# Revit family: Sink-Undermount-KOHLER-Caxton_Oval-K-2210
name_source: partatom
category: Plumbing Fixtures
revit_build: Autodesk Revit 2018 (Build: 20180329_1100(x64)
units: mm (PartAtom-declared; Revit-internal decimal feet)

## family parameters
Cut with Voids When Loaded = No
Host = Face
OmniClass Number = 23.45.05.14.14
OmniClass Title = Sinks/Lavatories
Part Type = Normal
Room Calculation Point = No
Round Connector Dimension = Use Diameter
Shared = No

## types (1)
- Kohler 2210IN-0
    CW Connection = No
    Default Elevation = 914 mm
    Description = Undercounter basin in white
    HW Connection = No
    Height = 187 mm
    Length = 416 mm
    Manufacturer = KOHLER Co.
    Material1 = Kohler-Vitreous_China-0-White
    Model = Kohler Caxton 2210IN-0
    Type Image = 2210in-0.tif
    URL = https://www.us.kohler.com
    Vent Connection = No
    Waste Connection = Yes
    Width = 494 mm

## geometry (parser evidence)
native form markers: Sweep x2
no freeform markers — native parametric forms only
